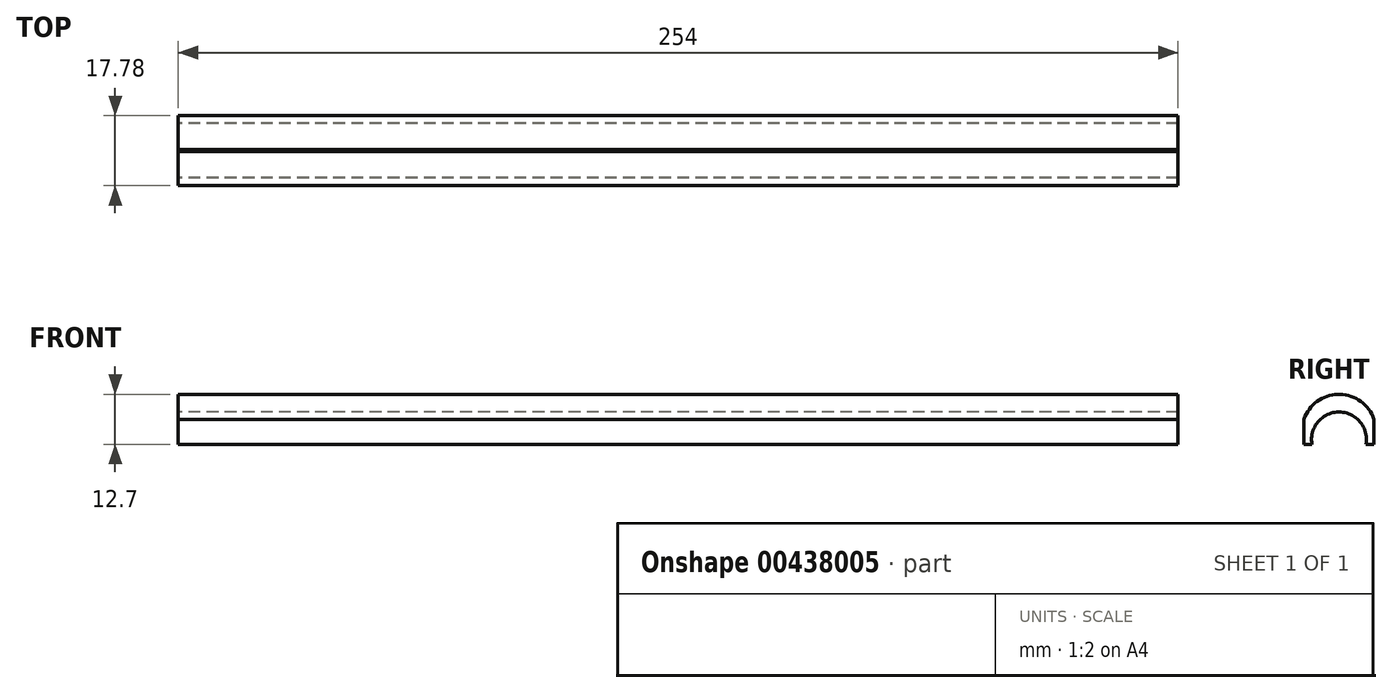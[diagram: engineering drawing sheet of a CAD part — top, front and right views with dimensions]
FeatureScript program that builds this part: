
annotation { "Feature Type Name" : "Feature", "Feature Type Description" : "" }
export const myFeature = defineFeature(function(context is Context, id is Id, definition is map)
    precondition{}
    {
        {
            var Q0;
            Q0=qCreatedBy(makeId("Top.planeOp"),FACE);
            var sketch = newSketch(context, id + "F0", { "sketchPlane" : qUnion([Q0])});
            skLineSegment(sketch, "E0.bottom", {"start": v(-116.95, 11.7) * mm, "end": v(137.05, 11.7) * mm});
            skLineSegment(sketch, "E0.top", {"start": v(-116.95, -6.07) * mm, "end": v(137.05, -6.07) * mm});
            skLineSegment(sketch, "E0.left", {"start": v(-116.95, 11.7) * mm, "end": v(-116.95, -6.07) * mm});
            skLineSegment(sketch, "E0.right", {"start": v(137.05, 11.7) * mm, "end": v(137.05, -6.07) * mm});
            skSolve(sketch);
        }
        {
            var Q0;
            Q0=makeQuery(id+"F0.imprint","IMPRINT",FACE,{"disambiguationData":[TD([[makeQuery(id+"F0.imprint","IMPRINT",EDGE,{"derivedFrom":sQuery(id+"F0.wireOp",EDGE,"E0.bottom")}),-1.0]])]});
            extrude(context, id + "F1", {"entities" : qUnion([Q0]), "depth" : 12.7 * mm});
        }
        {
            var Q0;
            Q0=makeQuery(id+"F1.opExtrude","SWEPT_FACE",FACE,{"disambiguationData":[OSD([sQuery(id+"F0.wireOp",EDGE,"E0.left")])]});
            var sketch = newSketch(context, id + "F2", { "sketchPlane" : qUnion([Q0])});
            skArc(sketch, "E1", {"start": v(6.07, 6.35) * mm, "mid": v(-2.82, 12.7) * mm, "end": v(-11.7, 6.35) * mm});
            skArc(sketch, "E2", {"start": v(4.04, 0) * mm, "mid": v(-2.82, 8.18) * mm, "end": v(-9.68, 0) * mm});
            skSolve(sketch);
        }
        {
            var Q0;
            {var subQ0=sQuery(id+"F2.wireOp",EDGE,"E1");var subQ1=sQuery(id+"F0.wireOp",EDGE,"E0.left");var subQ4=makeQuery(id+"F1.opExtrude","CAP_EDGE",EDGE,{"disambiguationData":[OSD([subQ1])],"isStart":false});var subQ5=makeQuery(id+"F2.imprint","INTERSECT",VERTEX,{"disambiguationData":[OD(1.0)],"derivedFrom":[subQ4,subQ0]});Q0=makeQuery(id+"F2.imprint","IMPRINT",FACE,{"disambiguationData":[TD([[makeQuery(id+"F2.imprint","IMPRINT",EDGE,{"disambiguationData":[TD([[subQ5,-1.0]])],"derivedFrom":subQ0}),-1.0]])]});}
            var Q1;
            {var subQ0=sQuery(id+"F2.wireOp",EDGE,"E1");var subQ1=sQuery(id+"F0.wireOp",EDGE,"E0.left");var subQ4=makeQuery(id+"F1.opExtrude","CAP_EDGE",EDGE,{"disambiguationData":[OSD([subQ1])],"isStart":false});var subQ5=makeQuery(id+"F2.imprint","INTERSECT",VERTEX,{"disambiguationData":[OD(0.0)],"derivedFrom":[subQ4,subQ0]});Q1=makeQuery(id+"F2.imprint","IMPRINT",FACE,{"disambiguationData":[TD([[makeQuery(id+"F2.imprint","IMPRINT",EDGE,{"disambiguationData":[TD([[subQ5,1.0]])],"derivedFrom":subQ0}),-1.0]])]});}
            var Q2;
            {var subQ0=sQuery(id+"F2.wireOp",EDGE,"E2");Q2=makeQuery(id+"F2.imprint","IMPRINT",FACE,{"disambiguationData":[TD([[makeQuery(id+"F2.imprint","IMPRINT",EDGE,{"derivedFrom":subQ0}),1.0]])]});}
            extrude(context, id + "F3", {"entities" : qUnion([Q0, Q1, Q2]), "operationType" : NewBodyOperationType.REMOVE, "oppositeDirection" : true, "depth" : 254 * mm});
        }
    });
